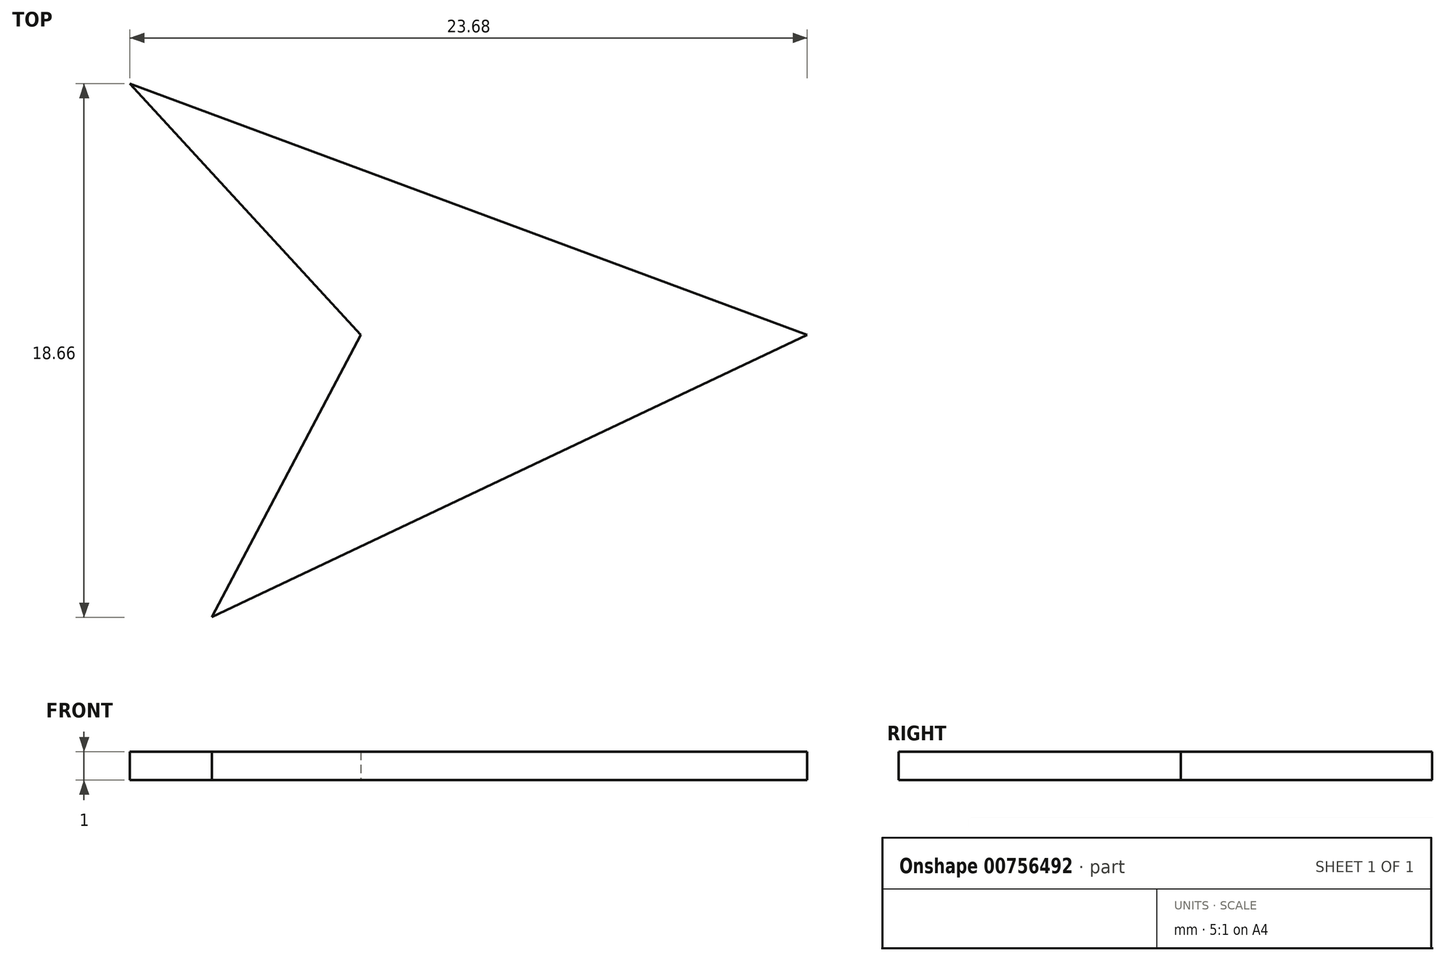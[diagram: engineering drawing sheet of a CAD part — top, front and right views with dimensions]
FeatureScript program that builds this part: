
annotation { "Feature Type Name" : "Feature", "Feature Type Description" : "" }
export const myFeature = defineFeature(function(context is Context, id is Id, definition is map)
    precondition{}
    {
        {
            var Q0;
            Q0=qCreatedBy(makeId("Top.planeOp"),FACE);
            var sketch = newSketch(context, id + "F0", { "sketchPlane" : qUnion([Q0])});
            skLineSegment(sketch, "E0", {"start": v(0, 0) * mm, "end": v(-8.07, 8.8) * mm});
            skLineSegment(sketch, "E1", {"start": v(-8.07, 8.8) * mm, "end": v(15.6, 0) * mm});
            skLineSegment(sketch, "E2", {"start": v(15.6, 0) * mm, "end": v(-5.2, -9.87) * mm});
            skLineSegment(sketch, "E3", {"start": v(-5.2, -9.87) * mm, "end": v(0, 0) * mm});
            skSolve(sketch);
        }
        {
            var Q0;
            Q0=makeQuery(id+"F0.imprint","IMPRINT",FACE,{"disambiguationData":[TD([[makeQuery(id+"F0.imprint","IMPRINT",EDGE,{"derivedFrom":sQuery(id+"F0.wireOp",EDGE,"E0")}),-1.0]])]});
            extrude(context, id + "F1", {"entities" : qUnion([Q0]), "depth" : 1 * mm, "offsetDistance" : 25 * mm});
        }
    });
